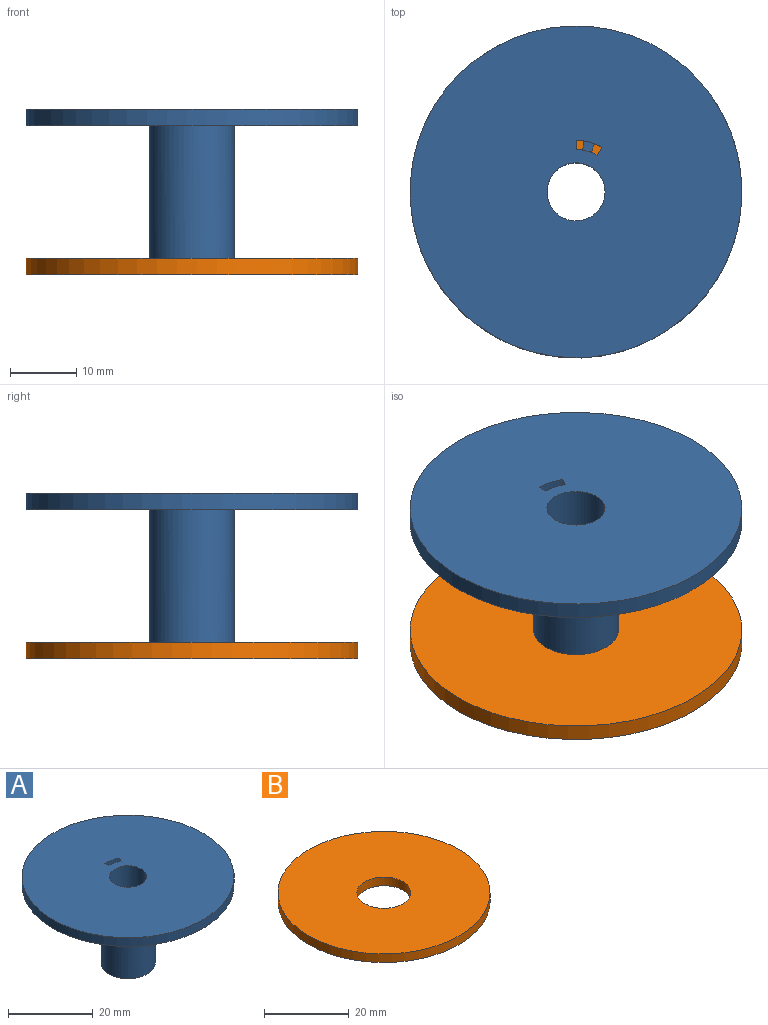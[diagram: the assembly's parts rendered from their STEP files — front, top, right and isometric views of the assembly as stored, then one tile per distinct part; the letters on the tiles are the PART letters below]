
ASSEMBLY  parts=2 mates=1
PART A: 12 faces, bbox 50x50x25 mm
  f0: cylinder r=7.77mm len=3.89mm, axis (0,0,1), area 8.5mm2, adj f1,f6,f7,f8,f9,f10,f11
  f1: plane 50x50mm, normal (0,0,1), area 1898.2mm2, adj f0,f2,f3,f5,f7,f8
  f2: cylinder r=4.38mm len=25mm, axis (0,0,-1), area 687.2mm2, adj f1,f4
  f3: cylinder r=6.38mm len=25mm, axis (0,0,-1), area 908.2mm2, adj f1,f4,f6,f7,f8,f9,f10,f11
  f4: plane 12.75x12.75mm, normal (0,0,-1), area 67.5mm2, adj f2,f3
  f5: cylinder r=25mm len=50mm, axis (0,0,-1), area 392.7mm2, adj f1,f6
  f6: plane 50x50mm, normal (0,0,-1), area 1832.7mm2, adj f0,f3,f5,f7,f8,f9,f10
  f7: plane 2.5x1.21mm, normal (-0.87,0.5,0), area 3.5mm2, adj f0,f1,f3,f6
  f8: plane 2.5x1.4mm, normal (1,0,0), area 3.5mm2, adj f0,f1,f3,f6
  f9: plane 1.38x1mm, normal (-0.99,0.16,0), area 1.4mm2, adj f0,f3,f6,f11
  f10: plane 1.31x1mm, normal (0.93,-0.36,0), area 1.4mm2, adj f0,f3,f6,f11
  f11: plane 1.8x1.73mm, normal (0,0,1), area 2.1mm2, adj f0,f3,f9,f10
PART B: 4 faces, bbox 50x50x2.5 mm
  f0: cylinder r=6.38mm len=12.75mm, axis (0,0,1), area 100.1mm2, adj f2,f3
  f1: cylinder r=25mm len=50mm, axis (0,0,1), area 392.7mm2, adj f2,f3
  f2: plane 50x50mm, normal (0,0,-1), area 1835.8mm2, adj f0,f1
  f3: plane 50x50mm, normal (0,0,1), area 1835.8mm2, adj f0,f1
PLACE A t=(11.14,1.99,3.33)mm
PLACE B t=(11.14,1.99,5.83)mm
MATE fastened A.f3 <-> B.f1  axis (0,0,-1) through (11.14,1.99,-7.92)mm
